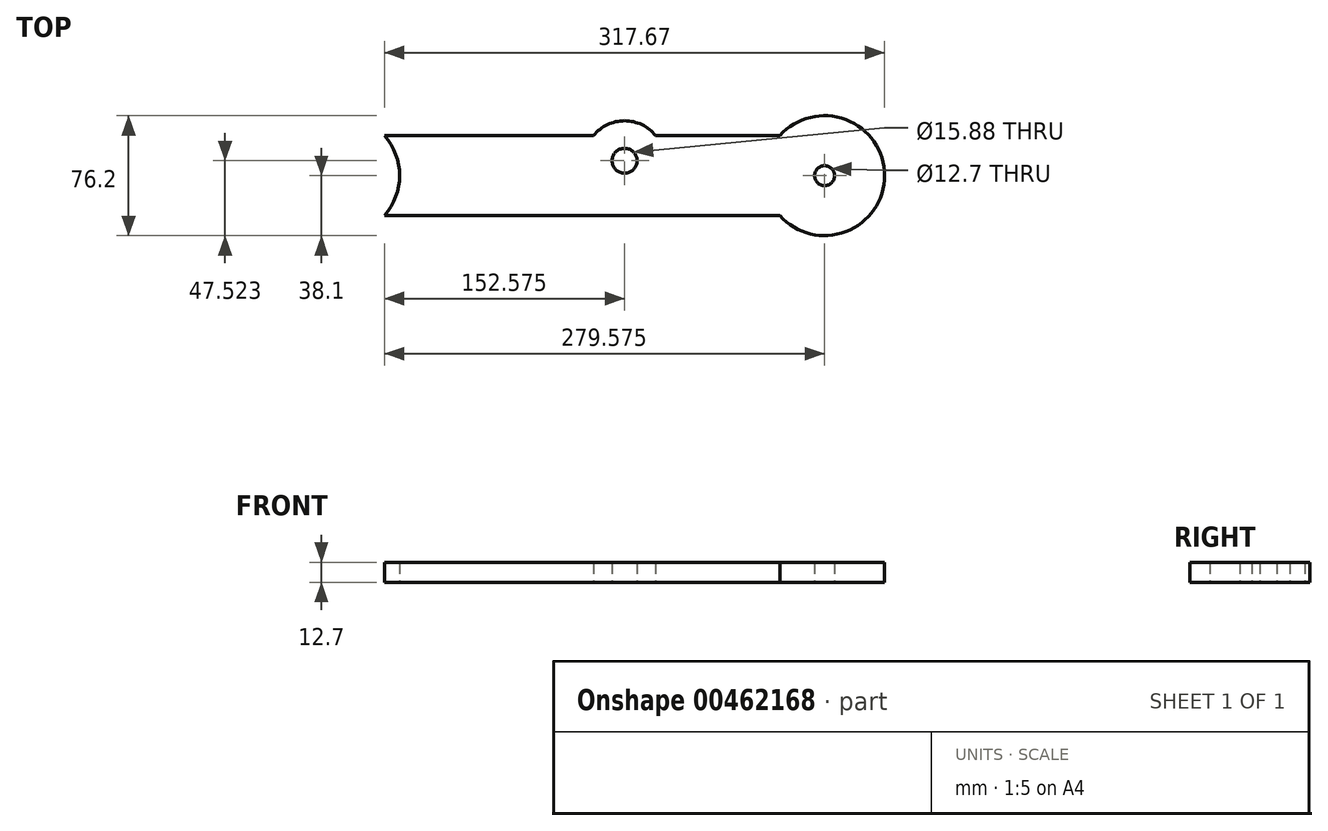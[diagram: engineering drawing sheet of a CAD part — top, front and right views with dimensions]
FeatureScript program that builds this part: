
annotation { "Feature Type Name" : "Feature", "Feature Type Description" : "" }
export const myFeature = defineFeature(function(context is Context, id is Id, definition is map)
    precondition{}
    {
        {
            var Q0;
            Q0=qCreatedBy(makeId("Top.planeOp"),FACE);
            var sketch = newSketch(context, id + "F0", { "sketchPlane" : qUnion([Q0])});
            skLineSegment(sketch, "E0.bottom", {"start": v(158.93, -25.4) * mm, "end": v(-92.25, -25.4) * mm});
            skLineSegment(sketch, "E0.top", {"start": v(158.93, 25.4) * mm, "end": v(-92.25, 25.4) * mm});
            skLineSegment(sketch, "E0.right", {"start": v(-212.73, -25.4) * mm, "end": v(-212.73, 25.4) * mm});
            skPoint(sketch, "E0.middle", {"position": v(0, 0) * mm});
            skLineSegment(sketch, "E1", {"start": v(-212.73, 0) * mm, "end": v(212.73, 0) * mm, "construction": true});
            skPoint(sketch, "E2", {"position": v(187.33, 0) * mm});
            skPoint(sketch, "E3", {"position": v(-120.65, 0) * mm});
            skPoint(sketch, "E4", {"position": v(-174.62, 0) * mm});
            skArc(sketch, "E5", {"start": v(-174.62, 38.1) * mm, "mid": v(-212.72, 0) * mm, "end": v(-174.62, -38.1) * mm});
            skCircle(sketch, "E6", {"center": v(187.33, 0) * mm, "radius": 38.1 * mm});
            skLineSegment(sketch, "E7", {"start": v(-174.62, 38.1) * mm, "end": v(-120.65, 38.1) * mm});
            skLineSegment(sketch, "E8", {"start": v(-174.62, -38.1) * mm, "end": v(-120.65, -38.1) * mm});
            skLineSegment(sketch, "E9.trimOffspring", {"start": v(-203.02, 25.4) * mm, "end": v(-212.73, 25.4) * mm});
            skArc(sketch, "E10.trimOffspring", {"start": v(-120.65, -38.1) * mm, "mid": v(-82.55, 0) * mm, "end": v(-120.65, 38.1) * mm});
            skLineSegment(sketch, "E11.trimOffspring", {"start": v(-203.02, -25.4) * mm, "end": v(-212.73, -25.4) * mm});
            skPoint(sketch, "E12.orphan", {"position": v(212.73, -25.4) * mm});
            skPoint(sketch, "E13.orphan", {"position": v(212.73, 25.4) * mm});
            skCircle(sketch, "E14", {"center": v(60.33, 9.42) * mm, "radius": 25.4 * mm});
            skCircle(sketch, "E15", {"center": v(187.33, 0) * mm, "radius": 6.35 * mm});
            skCircle(sketch, "E16", {"center": v(60.33, 9.42) * mm, "radius": 7.94 * mm});
            skCircle(sketch, "E17", {"center": v(-120.65, 0) * mm, "radius": 6.35 * mm});
            skCircle(sketch, "E18", {"center": v(-174.62, 0) * mm, "radius": 6.35 * mm});
            skSolve(sketch);
        }
        {
            var Q0;
            {var subQ5=sQuery(id+"F0.wireOp",EDGE,"E7");Q0=makeQuery(id+"F0.imprint","IMPRINT",FACE,{"disambiguationData":[TD([[makeQuery(id+"F0.imprint","IMPRINT",EDGE,{"derivedFrom":subQ5}),-1.0]])]});}
            var Q1;
            {var subQ0=sQuery(id+"F0.wireOp",EDGE,"E0.bottom");Q1=makeQuery(id+"F0.imprint","IMPRINT",FACE,{"disambiguationData":[TD([[makeQuery(id+"F0.imprint","IMPRINT",EDGE,{"derivedFrom":subQ0}),-1.0]])]});}
            var Q2;
            {var subQ0=sQuery(id+"F0.wireOp",EDGE,"E6");var subQ1=makeQuery(id+"F0.imprint","INTERSECT",VERTEX,{"derivedFrom":[sQuery(id+"F0.wireOp",EDGE,"E0.bottom"),subQ0]});Q2=makeQuery(id+"F0.imprint","IMPRINT",FACE,{"disambiguationData":[TD([[makeQuery(id+"F0.imprint","IMPRINT",EDGE,{"disambiguationData":[TD([[subQ1,1.0]])],"derivedFrom":subQ0}),1.0]])]});}
            var Q3;
            Q3=makeQuery(id+"F0.imprint","IMPRINT",FACE,{"disambiguationData":[TD([[makeQuery(id+"F0.imprint","IMPRINT",EDGE,{"derivedFrom":sQuery(id+"F0.wireOp",EDGE,"E16")}),-1.0]])]});
            var Q4;
            {var subQ0=sQuery(id+"F0.wireOp",EDGE,"E14");var subQ1=sQuery(id+"F0.wireOp",EDGE,"E0.top");var subQ2=makeQuery(id+"F0.imprint","INTERSECT",VERTEX,{"disambiguationData":[OD(0.0)],"derivedFrom":[subQ1,subQ0]});Q4=makeQuery(id+"F0.imprint","IMPRINT",FACE,{"disambiguationData":[TD([[makeQuery(id+"F0.imprint","IMPRINT",EDGE,{"disambiguationData":[TD([[subQ2,-1.0]])],"derivedFrom":subQ1}),-1.0]])]});}
            extrude(context, id + "F1", {"entities" : qUnion([Q0, Q1, Q2, Q3, Q4]), "depth" : 12.7 * mm, "symmetric" : true});
        }
        {
            var Q0;
            Q0=makeQuery(id+"F1.opExtrude","CAP_FACE",FACE,{"disambiguationData":[OSD([sQuery(id+"F0.wireOp",EDGE,"E0.bottom"),sQuery(id+"F0.wireOp",EDGE,"E0.top"),sQuery(id+"F0.wireOp",EDGE,"E5"),sQuery(id+"F0.wireOp",EDGE,"E6"),sQuery(id+"F0.wireOp",EDGE,"E7"),sQuery(id+"F0.wireOp",EDGE,"E8"),sQuery(id+"F0.wireOp",EDGE,"E10.trimOffspring"),sQuery(id+"F0.wireOp",EDGE,"E14"),sQuery(id+"F0.wireOp",EDGE,"E15"),sQuery(id+"F0.wireOp",EDGE,"E16"),sQuery(id+"F0.wireOp",EDGE,"E17"),sQuery(id+"F0.wireOp",EDGE,"E18")])],"isStart":true});
            var sketch = newSketch(context, id + "F2", { "sketchPlane" : qUnion([Q0])});
            skCircle(sketch, "E19", {"center": v(-174.62, 0) * mm, "radius": 11.11 * mm});
            skSolve(sketch);
        }
        {
            var Q0;
            Q0=qSketchRegion(id+"F2",true);
            extrude(context, id + "F3", {"entities" : qUnion([Q0]), "operationType" : NewBodyOperationType.REMOVE, "oppositeDirection" : true, "depth" : 3.17 * mm});
        }
    });
